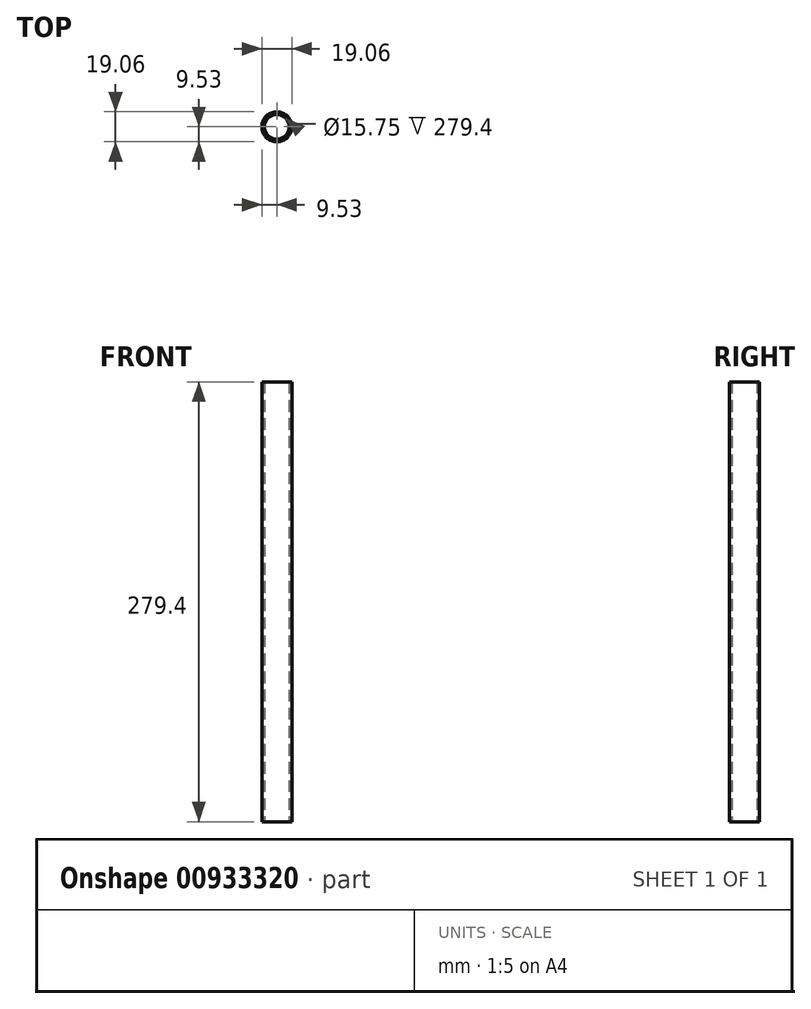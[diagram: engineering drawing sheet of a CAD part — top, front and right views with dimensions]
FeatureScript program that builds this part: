
annotation { "Feature Type Name" : "Feature", "Feature Type Description" : "" }
export const myFeature = defineFeature(function(context is Context, id is Id, definition is map)
    precondition{}
    {
        {
            var Q0;
            Q0=qCreatedBy(makeId("Top.planeOp"),FACE);
            var sketch = newSketch(context, id + "F0", { "sketchPlane" : qUnion([Q0])});
            skCircle(sketch, "E0", {"center": v(0, 0) * mm, "radius": 9.53 * mm});
            skCircle(sketch, "E1", {"center": v(0, 0) * mm, "radius": 7.87 * mm});
            skSolve(sketch);
        }
        {
            var Q0;
            Q0=makeQuery(id+"F0.imprint","IMPRINT",FACE,{"disambiguationData":[TD([[makeQuery(id+"F0.imprint","IMPRINT",EDGE,{"derivedFrom":sQuery(id+"F0.wireOp",EDGE,"E0")}),1.0]])]});
            extrude(context, id + "F1", {"entities" : qUnion([Q0]), "depth" : 279.4 * mm, "offsetDistance" : 25.4 * mm});
        }
    });
